# Revit family: Skylight-VELUX AUS_VCS-curb_mounted-solar-venting
name_source: partatom
category: Windows
units: mm (PartAtom-declared; Revit-internal decimal feet)

## family parameters
Always vertical = No
Cut with Voids When Loaded = No
Host = Roof
OmniClass Number = 23.30.30.14
OmniClass Title = Unit Skylights
Room Calculation Point = No
Shared = No

## types (7) — shared parameters
Assembly Code = B3020110
Curb Height (3 1/2" minimum) = 89 mm
Description = Solar venting curb mounted skylight
Drawings & Specifications (+Codes & Installation Instructions) = http://www.veluxusa.com
Frame = ABS - Acrylonitrile-Butadiene-Styrene
Frame finish = Aluminum - Lacquered - Kynar 500 top finish - Neutral Gray
Glazing Material = Glass-VELUX_04-Laminated
Manufacturer = VELUX
Maximum Roof Pitch = 60 degrees
Minimum Roof Pitch = 0 degrees
Model = VCS
SHGC - Solar Heat Gain Coefficient (04) = 0.24
SHGC - Solar Heat Gain Coefficient (06) = 0.24
SHGC - Solar Heat Gain Coefficient (08) = 0.23
SHGC - Solar Heat Gain Coefficient (10) = 0.24
SHGC - Solar Heat Gain Coefficient (9993) = 0.22
SHGC - Solar Heat Gain Coefficient (9994) = 0.22
Type Comments = Designed for curb mounted installations
U-Factor (04) = 0.53
U-Factor (06) = 0.51
U-Factor (08) = 0.53
U-Factor (10) = 0.51
U-Factor (9993) = 0.49
U-Factor (9994) = 0.48
URL = http://www.veluxusa.com
VELUX Flashing systems = ECL step flashing (low profile roof), ECW tile flashing (high profile roof)
VELUX Flashing systems URL = http://www.veluxusa.com
VT - Visible Transmittance (04) = 0.55
VT - Visible Transmittance (06) = 0.54
VT - Visible Transmittance (08) = 0.40
VT - Visible Transmittance (10) = 0.54
VT - Visible Transmittance (9993) = 0.50
VT - Visible Transmittance (9994) = 0.49

## per-type parameters (varying)
| type | Height | Rough Height | Rough Width | VELUX Glazing options | Width |
| VCS 2222 | 648 mm | 572 mm | 572 mm | Laminated (04), Impact (06), White Laminated (08), Snowload (10), Energy Tempered (9993), Energy Laminated (9994) | 648 mm |
| VCS 2234 | 953 mm | 876 mm | 572 mm | Laminated (04), Impact (06), White Laminated (08), Snowload (10), Energy Tempered (9993), Energy Laminated (9994) | 648 mm |
| VCS 2246 | 1257 mm | 1181 mm | 572 mm | Laminated (04), Impact (06), White Laminated (08), Snowload (10), Energy Tempered (9993), Energy Laminated (9994) | 648 mm |
| VCS 3030 | 851 mm | 775 mm | 775 mm | Laminated (04), Impact (06), White Laminated (08), Snowload (10), Energy Tempered (9993), Energy Laminated (9994) | 851 mm |
| VCS 3046 | 1257 mm | 1181 mm | 775 mm | Laminated (04), Impact (06), White Laminated (08), Snowload (10), Energy Tempered (9993), Energy Laminated (9994) | 851 mm |
| VCS 4622 | 648 mm | 572 mm | 1181 mm | Lamianted (04), Impact (06), White Laminated (08), Snowload (10), Energy Tempered (9993), Energy Laminated (9994) | 1257 mm |
| VCS 4646 | 1257 mm | 1181 mm | 1181 mm | Laminated (04), Impact (06), White Laminated (08), Snowload (10), Energy Tempered 99993), Energy Laminated (9994) | 1257 mm |
